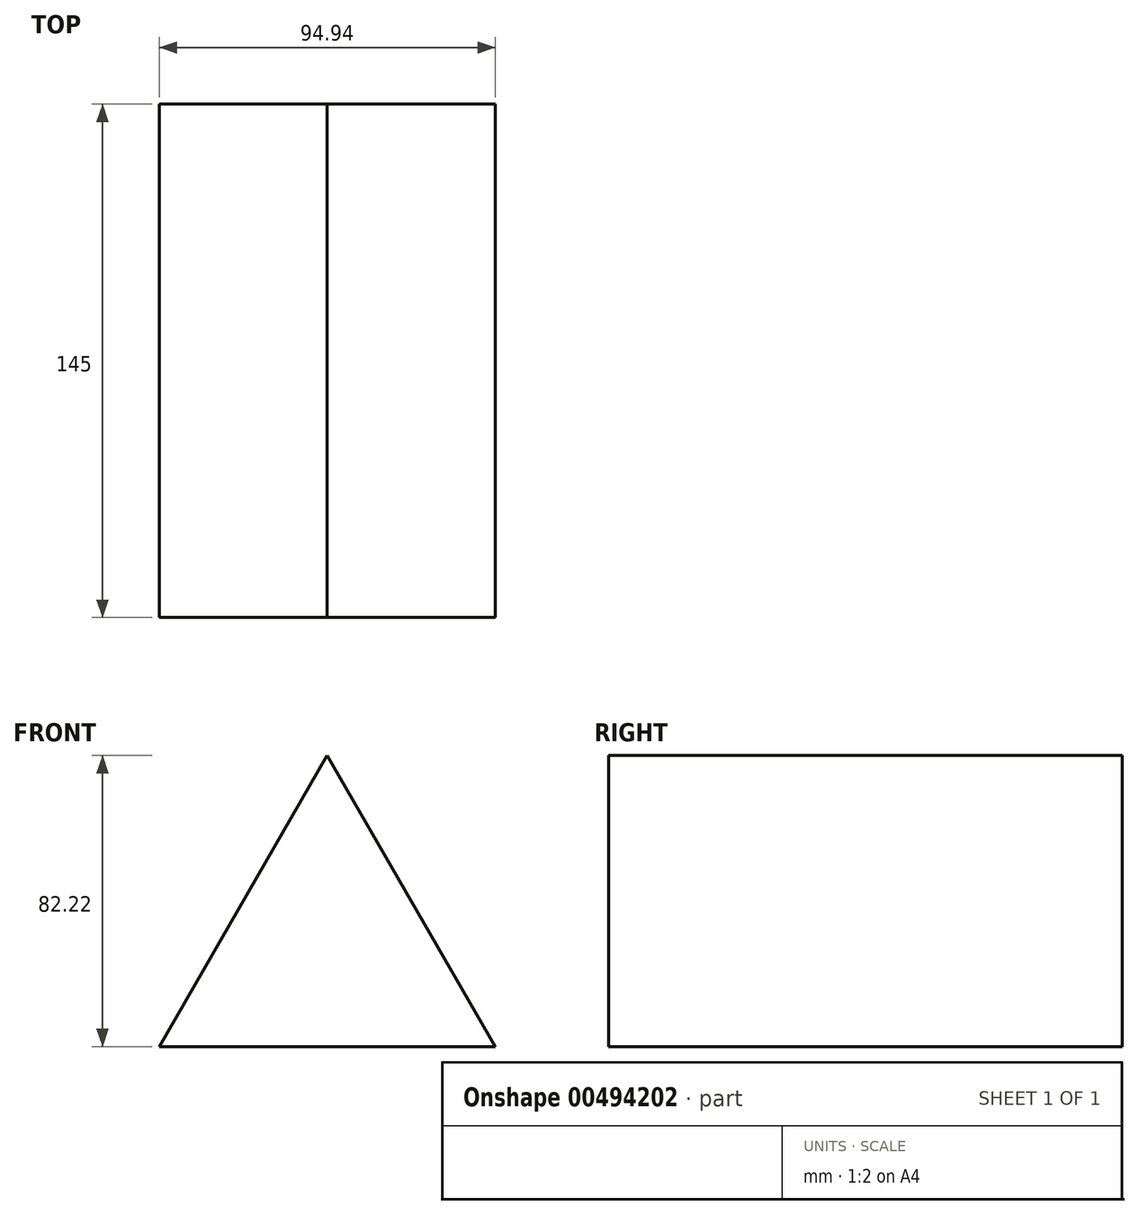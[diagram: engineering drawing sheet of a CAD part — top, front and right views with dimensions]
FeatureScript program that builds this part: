
annotation { "Feature Type Name" : "Feature", "Feature Type Description" : "" }
export const myFeature = defineFeature(function(context is Context, id is Id, definition is map)
    precondition{}
    {
        {
            var Q0;
            Q0=qCreatedBy(makeId("Front.planeOp"),FACE);
            var sketch = newSketch(context, id + "F0", { "sketchPlane" : qUnion([Q0])});
            skCircle(sketch, "E0.cCircle", {"center": v(0, 0) * mm, "radius": 54.81 * mm, "construction": true});
            skLineSegment(sketch, "E0.0", {"start": v(0, 54.81) * mm, "end": v(47.47, -27.4) * mm});
            skLineSegment(sketch, "E0.1", {"start": v(47.47, -27.4) * mm, "end": v(-47.47, -27.4) * mm});
            skLineSegment(sketch, "E0.2", {"start": v(-47.47, -27.4) * mm, "end": v(0, 54.81) * mm});
            skSolve(sketch);
        }
        {
            var Q0;
            Q0=makeQuery(id+"F0.imprint","IMPRINT",FACE,{"disambiguationData":[TD([[makeQuery(id+"F0.imprint","IMPRINT",EDGE,{"derivedFrom":sQuery(id+"F0.wireOp",EDGE,"E0.0")}),-1.0]])]});
            extrude(context, id + "F1", {"entities" : qUnion([Q0]), "depth" : 145 * mm});
        }
    });
